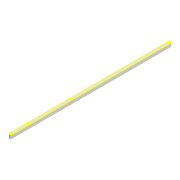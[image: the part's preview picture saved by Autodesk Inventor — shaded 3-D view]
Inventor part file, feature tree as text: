
AUTODESK INVENTOR PART (.ipt)
format: ipt  version: 2022 (Build 260153000, 153)  size: 98,304 bytes
history: native  units: mm
features: sketch x2, extrude x1, projected_geometry x1
ambient origin geometry x8: Origin, YZ Plane, XZ Plane, XY Plane, X Axis, Y Axis, Z Axis, Center Point
bodies: Solid1 (feature_tree)
feature tree (4):
  extrude  "Extrusion1"  Depth=6.0mm
  sketch  "Sketch2"  dims[d2=3.0mm d3=3.0mm d4=8.0mm d5=0.0mm d6=3.0mm d7=131.233mm d8=3.0mm d9=37.934mm]
  sketch  "Sketch1"  dims[d0=347.765mm d1=6.0mm]
  projected_geometry  "Projected Loop1"
